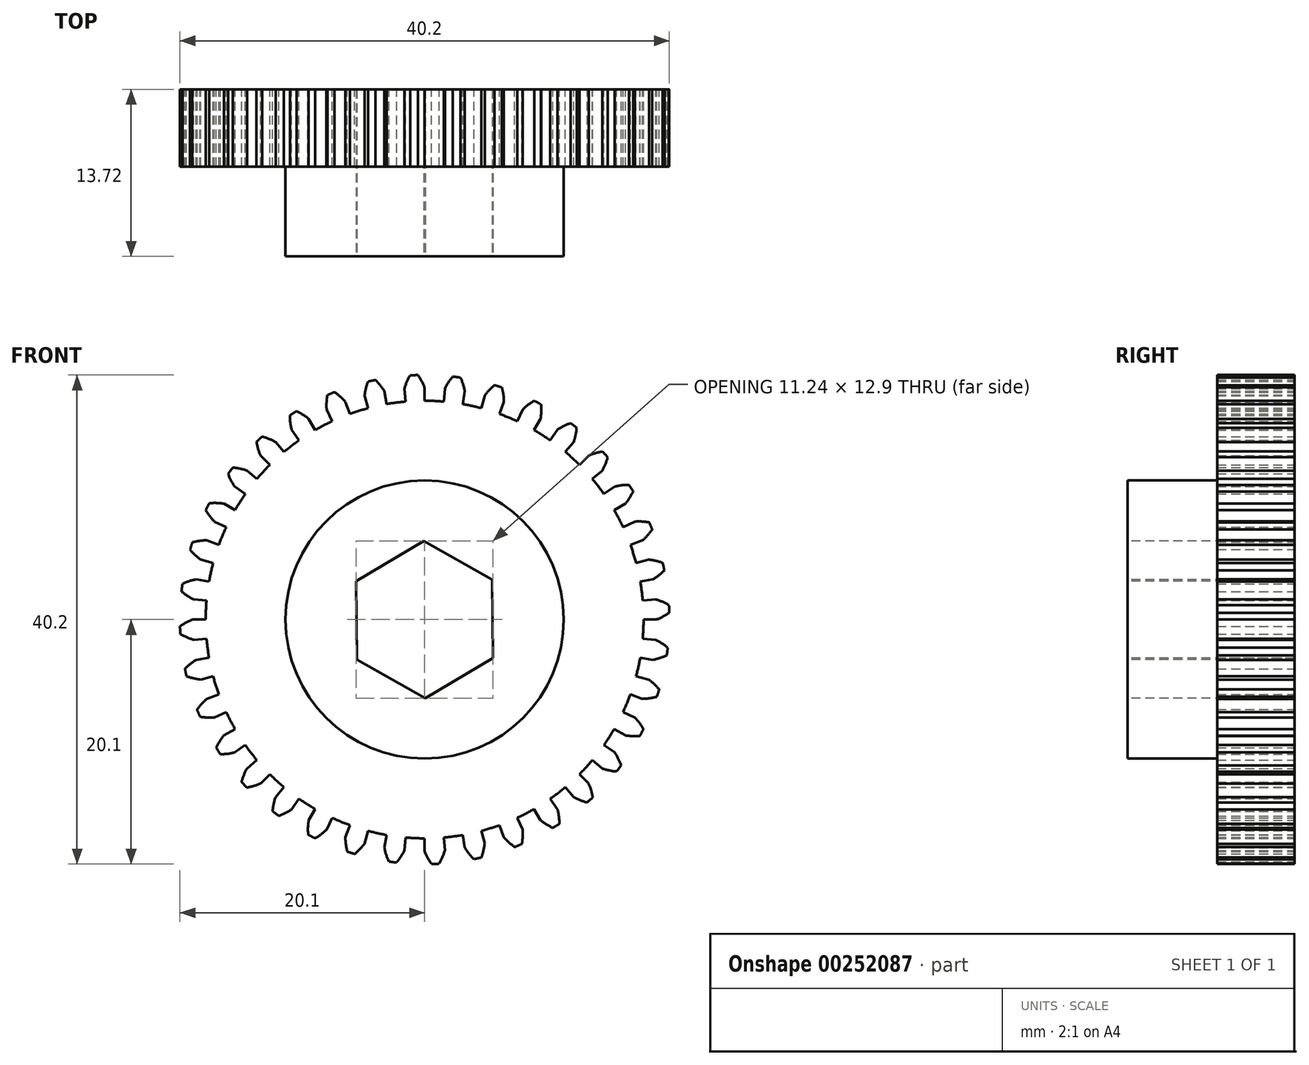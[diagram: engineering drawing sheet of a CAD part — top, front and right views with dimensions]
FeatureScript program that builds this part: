
annotation { "Feature Type Name" : "Feature", "Feature Type Description" : "" }
export const myFeature = defineFeature(function(context is Context, id is Id, definition is map)
    precondition{}
    {
        {
            var Q0;
            Q0=qCreatedBy(makeId("Front.planeOp"),FACE);
            var sketch = newSketch(context, id + "F0", { "sketchPlane" : qUnion([Q0])});
            skArc(sketch, "E0", {"start": v(1.57, 17.91) * mm, "mid": v(0.78, 17.97) * mm, "end": v(0, 17.98) * mm});
            skArc(sketch, "E1", {"start": v(-0.56, 20.1) * mm, "mid": v(-0.72, 20.1) * mm, "end": v(-0.88, 20.08) * mm});
            skLineSegment(sketch, "E2", {"start": v(0, 17.98) * mm, "end": v(0, 19.05) * mm});
            skLineSegment(sketch, "E3", {"start": v(0, 19.05) * mm, "end": v(0, 17.98) * mm});
            skArc(sketch, "E4.trimOffspring", {"start": v(0, 19.05) * mm, "mid": v(-0.25, 19.6) * mm, "end": v(-0.56, 20.1) * mm});
            skPoint(sketch, "E5", {"position": v(0, 17.98) * mm});
            skArc(sketch, "E6.MirrorCS", {"start": v(-1.2, 20.07) * mm, "mid": v(-1.03, 20.08) * mm, "end": v(-0.88, 20.08) * mm});
            skArc(sketch, "E7.MirrorCS", {"start": v(-1.66, 18.98) * mm, "mid": v(-1.46, 19.54) * mm, "end": v(-1.2, 20.07) * mm});
            skLineSegment(sketch, "E8.MirrorCS", {"start": v(-1.66, 18.98) * mm, "end": v(-1.57, 17.91) * mm});
            skLineSegment(sketch, "E9.1.0", {"start": v(-4.93, 18.4) * mm, "end": v(-4.65, 17.37) * mm});
            skArc(sketch, "E9.1.1", {"start": v(-4.93, 18.4) * mm, "mid": v(-4.83, 18.99) * mm, "end": v(-4.66, 19.56) * mm});
            skArc(sketch, "E9.1.2", {"start": v(-3.3, 18.76) * mm, "mid": v(-3.65, 19.25) * mm, "end": v(-4.04, 19.7) * mm});
            skLineSegment(sketch, "E9.1.3", {"start": v(-3.3, 18.76) * mm, "end": v(-3.12, 17.7) * mm});
            skPoint(sketch, "E9.1.4", {"position": v(-3.12, 17.7) * mm});
            skLineSegment(sketch, "E9.1.5", {"start": v(-3.12, 17.7) * mm, "end": v(-3.3, 18.76) * mm});
            skArc(sketch, "E9.1.6", {"start": v(-4.66, 19.56) * mm, "mid": v(-4.5, 19.6) * mm, "end": v(-4.35, 19.63) * mm});
            skArc(sketch, "E9.1.7", {"start": v(-4.04, 19.7) * mm, "mid": v(-4.2, 19.66) * mm, "end": v(-4.35, 19.63) * mm});
            skLineSegment(sketch, "E9.2.0", {"start": v(-8.05, 17.27) * mm, "end": v(-7.6, 16.3) * mm});
            skArc(sketch, "E9.2.1", {"start": v(-8.05, 17.27) * mm, "mid": v(-8.05, 17.86) * mm, "end": v(-7.98, 18.45) * mm});
            skArc(sketch, "E9.2.2", {"start": v(-6.52, 17.9) * mm, "mid": v(-6.93, 18.32) * mm, "end": v(-7.4, 18.7) * mm});
            skLineSegment(sketch, "E9.2.3", {"start": v(-6.52, 17.9) * mm, "end": v(-6.15, 16.9) * mm});
            skPoint(sketch, "E9.2.4", {"position": v(-6.15, 16.9) * mm});
            skLineSegment(sketch, "E9.2.5", {"start": v(-6.15, 16.9) * mm, "end": v(-6.52, 17.9) * mm});
            skArc(sketch, "E9.2.6", {"start": v(-7.98, 18.45) * mm, "mid": v(-7.84, 18.51) * mm, "end": v(-7.7, 18.57) * mm});
            skArc(sketch, "E9.2.7", {"start": v(-7.4, 18.7) * mm, "mid": v(-7.55, 18.63) * mm, "end": v(-7.7, 18.57) * mm});
            skLineSegment(sketch, "E9.3.0", {"start": v(-10.93, 15.6) * mm, "end": v(-10.31, 14.73) * mm});
            skArc(sketch, "E9.3.1", {"start": v(-10.93, 15.6) * mm, "mid": v(-11.03, 16.19) * mm, "end": v(-11.07, 16.78) * mm});
            skArc(sketch, "E9.3.2", {"start": v(-9.52, 16.5) * mm, "mid": v(-10, 16.84) * mm, "end": v(-10.53, 17.12) * mm});
            skLineSegment(sketch, "E9.3.3", {"start": v(-9.52, 16.5) * mm, "end": v(-9, 15.57) * mm});
            skPoint(sketch, "E9.3.4", {"position": v(-9, 15.57) * mm});
            skLineSegment(sketch, "E9.3.5", {"start": v(-9, 15.57) * mm, "end": v(-9.53, 16.5) * mm});
            skArc(sketch, "E9.3.6", {"start": v(-11.07, 16.78) * mm, "mid": v(-10.93, 16.87) * mm, "end": v(-10.8, 16.96) * mm});
            skArc(sketch, "E9.3.7", {"start": v(-10.53, 17.12) * mm, "mid": v(-10.67, 17.04) * mm, "end": v(-10.8, 16.96) * mm});
            skLineSegment(sketch, "E9.4.0", {"start": v(-13.47, 13.47) * mm, "end": v(-12.72, 12.72) * mm});
            skArc(sketch, "E9.4.1", {"start": v(-13.47, 13.47) * mm, "mid": v(-13.68, 14.03) * mm, "end": v(-13.81, 14.6) * mm});
            skArc(sketch, "E9.4.2", {"start": v(-12.25, 14.6) * mm, "mid": v(-12.78, 14.85) * mm, "end": v(-13.35, 15.03) * mm});
            skLineSegment(sketch, "E9.4.3", {"start": v(-12.25, 14.6) * mm, "end": v(-11.56, 13.78) * mm});
            skPoint(sketch, "E9.4.4", {"position": v(-11.56, 13.78) * mm});
            skLineSegment(sketch, "E9.4.5", {"start": v(-11.56, 13.78) * mm, "end": v(-12.25, 14.6) * mm});
            skArc(sketch, "E9.4.6", {"start": v(-13.81, 14.6) * mm, "mid": v(-13.7, 14.72) * mm, "end": v(-13.58, 14.82) * mm});
            skArc(sketch, "E9.4.7", {"start": v(-13.35, 15.03) * mm, "mid": v(-13.47, 14.93) * mm, "end": v(-13.58, 14.82) * mm});
            skLineSegment(sketch, "E9.5.0", {"start": v(-15.6, 10.93) * mm, "end": v(-14.73, 10.31) * mm});
            skArc(sketch, "E9.5.1", {"start": v(-15.6, 10.93) * mm, "mid": v(-15.9, 11.44) * mm, "end": v(-16.14, 11.99) * mm});
            skArc(sketch, "E9.5.2", {"start": v(-14.6, 12.25) * mm, "mid": v(-15.17, 12.4) * mm, "end": v(-15.76, 12.49) * mm});
            skLineSegment(sketch, "E9.5.3", {"start": v(-14.6, 12.25) * mm, "end": v(-13.78, 11.56) * mm});
            skPoint(sketch, "E9.5.4", {"position": v(-13.78, 11.56) * mm});
            skLineSegment(sketch, "E9.5.5", {"start": v(-13.78, 11.56) * mm, "end": v(-14.6, 12.25) * mm});
            skArc(sketch, "E9.5.6", {"start": v(-16.14, 11.99) * mm, "mid": v(-16.05, 12.11) * mm, "end": v(-15.95, 12.24) * mm});
            skArc(sketch, "E9.5.7", {"start": v(-15.76, 12.49) * mm, "mid": v(-15.85, 12.36) * mm, "end": v(-15.95, 12.24) * mm});
            skLineSegment(sketch, "E9.6.0", {"start": v(-17.27, 8.05) * mm, "end": v(-16.3, 7.6) * mm});
            skArc(sketch, "E9.6.1", {"start": v(-17.27, 8.05) * mm, "mid": v(-17.65, 8.5) * mm, "end": v(-17.98, 9) * mm});
            skArc(sketch, "E9.6.2", {"start": v(-16.5, 9.53) * mm, "mid": v(-17.09, 9.58) * mm, "end": v(-17.68, 9.56) * mm});
            skLineSegment(sketch, "E9.6.3", {"start": v(-16.5, 9.53) * mm, "end": v(-15.57, 9) * mm});
            skPoint(sketch, "E9.6.4", {"position": v(-15.57, 9) * mm});
            skLineSegment(sketch, "E9.6.5", {"start": v(-15.57, 9) * mm, "end": v(-16.5, 9.53) * mm});
            skArc(sketch, "E9.6.6", {"start": v(-17.98, 9) * mm, "mid": v(-17.9, 9.14) * mm, "end": v(-17.83, 9.28) * mm});
            skArc(sketch, "E9.6.7", {"start": v(-17.68, 9.56) * mm, "mid": v(-17.76, 9.42) * mm, "end": v(-17.83, 9.28) * mm});
            skLineSegment(sketch, "E9.7.0", {"start": v(-18.4, 4.93) * mm, "end": v(-17.37, 4.65) * mm});
            skArc(sketch, "E9.7.1", {"start": v(-18.4, 4.93) * mm, "mid": v(-18.86, 5.3) * mm, "end": v(-19.27, 5.74) * mm});
            skArc(sketch, "E9.7.2", {"start": v(-17.9, 6.52) * mm, "mid": v(-18.5, 6.47) * mm, "end": v(-19.08, 6.35) * mm});
            skLineSegment(sketch, "E9.7.3", {"start": v(-17.9, 6.52) * mm, "end": v(-16.9, 6.15) * mm});
            skPoint(sketch, "E9.7.4", {"position": v(-16.9, 6.15) * mm});
            skLineSegment(sketch, "E9.7.5", {"start": v(-16.9, 6.15) * mm, "end": v(-17.9, 6.52) * mm});
            skArc(sketch, "E9.7.6", {"start": v(-19.27, 5.74) * mm, "mid": v(-19.22, 5.9) * mm, "end": v(-19.17, 6.05) * mm});
            skArc(sketch, "E9.7.7", {"start": v(-19.08, 6.35) * mm, "mid": v(-19.13, 6.2) * mm, "end": v(-19.17, 6.05) * mm});
            skLineSegment(sketch, "E9.8.0", {"start": v(-18.98, 1.66) * mm, "end": v(-17.91, 1.57) * mm});
            skArc(sketch, "E9.8.1", {"start": v(-18.98, 1.66) * mm, "mid": v(-19.5, 1.95) * mm, "end": v(-19.97, 2.31) * mm});
            skArc(sketch, "E9.8.2", {"start": v(-18.76, 3.3) * mm, "mid": v(-19.34, 3.16) * mm, "end": v(-19.89, 2.94) * mm});
            skLineSegment(sketch, "E9.8.3", {"start": v(-18.76, 3.3) * mm, "end": v(-17.7, 3.12) * mm});
            skPoint(sketch, "E9.8.4", {"position": v(-17.7, 3.12) * mm});
            skLineSegment(sketch, "E9.8.5", {"start": v(-17.7, 3.12) * mm, "end": v(-18.76, 3.3) * mm});
            skArc(sketch, "E9.8.6", {"start": v(-19.97, 2.31) * mm, "mid": v(-19.95, 2.47) * mm, "end": v(-19.93, 2.62) * mm});
            skArc(sketch, "E9.8.7", {"start": v(-19.89, 2.94) * mm, "mid": v(-19.91, 2.78) * mm, "end": v(-19.93, 2.62) * mm});
            skLineSegment(sketch, "E9.9.0", {"start": v(-18.98, -1.66) * mm, "end": v(-17.91, -1.57) * mm});
            skArc(sketch, "E9.9.1", {"start": v(-18.98, -1.66) * mm, "mid": v(-19.54, -1.46) * mm, "end": v(-20.07, -1.2) * mm});
            skArc(sketch, "E9.9.2", {"start": v(-19.05, 0) * mm, "mid": v(-19.6, -0.25) * mm, "end": v(-20.1, -0.56) * mm});
            skLineSegment(sketch, "E9.9.3", {"start": v(-19.05, 0) * mm, "end": v(-17.98, 0) * mm});
            skPoint(sketch, "E9.9.4", {"position": v(-17.98, 0) * mm});
            skLineSegment(sketch, "E9.9.5", {"start": v(-17.98, 0) * mm, "end": v(-19.05, 0) * mm});
            skArc(sketch, "E9.9.6", {"start": v(-20.07, -1.2) * mm, "mid": v(-20.08, -1.03) * mm, "end": v(-20.08, -0.88) * mm});
            skArc(sketch, "E9.9.7", {"start": v(-20.1, -0.56) * mm, "mid": v(-20.1, -0.72) * mm, "end": v(-20.08, -0.88) * mm});
            skLineSegment(sketch, "E9.10.0", {"start": v(-18.4, -4.93) * mm, "end": v(-17.37, -4.65) * mm});
            skArc(sketch, "E9.10.1", {"start": v(-18.4, -4.93) * mm, "mid": v(-18.99, -4.83) * mm, "end": v(-19.56, -4.66) * mm});
            skArc(sketch, "E9.10.2", {"start": v(-18.76, -3.3) * mm, "mid": v(-19.25, -3.65) * mm, "end": v(-19.7, -4.04) * mm});
            skLineSegment(sketch, "E9.10.3", {"start": v(-18.76, -3.3) * mm, "end": v(-17.7, -3.12) * mm});
            skPoint(sketch, "E9.10.4", {"position": v(-17.7, -3.12) * mm});
            skLineSegment(sketch, "E9.10.5", {"start": v(-17.7, -3.12) * mm, "end": v(-18.76, -3.3) * mm});
            skArc(sketch, "E9.10.6", {"start": v(-19.56, -4.66) * mm, "mid": v(-19.6, -4.5) * mm, "end": v(-19.63, -4.35) * mm});
            skArc(sketch, "E9.10.7", {"start": v(-19.7, -4.04) * mm, "mid": v(-19.66, -4.2) * mm, "end": v(-19.63, -4.35) * mm});
            skLineSegment(sketch, "E9.11.0", {"start": v(-17.27, -8.05) * mm, "end": v(-16.3, -7.6) * mm});
            skArc(sketch, "E9.11.1", {"start": v(-17.27, -8.05) * mm, "mid": v(-17.86, -8.05) * mm, "end": v(-18.45, -7.98) * mm});
            skArc(sketch, "E9.11.2", {"start": v(-17.9, -6.52) * mm, "mid": v(-18.32, -6.93) * mm, "end": v(-18.7, -7.4) * mm});
            skLineSegment(sketch, "E9.11.3", {"start": v(-17.9, -6.52) * mm, "end": v(-16.9, -6.15) * mm});
            skPoint(sketch, "E9.11.4", {"position": v(-16.9, -6.15) * mm});
            skLineSegment(sketch, "E9.11.5", {"start": v(-16.9, -6.15) * mm, "end": v(-17.9, -6.52) * mm});
            skArc(sketch, "E9.11.6", {"start": v(-18.45, -7.98) * mm, "mid": v(-18.51, -7.84) * mm, "end": v(-18.57, -7.7) * mm});
            skArc(sketch, "E9.11.7", {"start": v(-18.7, -7.4) * mm, "mid": v(-18.63, -7.55) * mm, "end": v(-18.57, -7.7) * mm});
            skLineSegment(sketch, "E9.12.0", {"start": v(-15.6, -10.93) * mm, "end": v(-14.73, -10.31) * mm});
            skArc(sketch, "E9.12.1", {"start": v(-15.6, -10.93) * mm, "mid": v(-16.19, -11.03) * mm, "end": v(-16.78, -11.07) * mm});
            skArc(sketch, "E9.12.2", {"start": v(-16.5, -9.52) * mm, "mid": v(-16.84, -10) * mm, "end": v(-17.12, -10.53) * mm});
            skLineSegment(sketch, "E9.12.3", {"start": v(-16.5, -9.52) * mm, "end": v(-15.57, -9) * mm});
            skPoint(sketch, "E9.12.4", {"position": v(-15.57, -9) * mm});
            skLineSegment(sketch, "E9.12.5", {"start": v(-15.57, -9) * mm, "end": v(-16.5, -9.53) * mm});
            skArc(sketch, "E9.12.6", {"start": v(-16.78, -11.07) * mm, "mid": v(-16.87, -10.93) * mm, "end": v(-16.96, -10.8) * mm});
            skArc(sketch, "E9.12.7", {"start": v(-17.12, -10.53) * mm, "mid": v(-17.04, -10.67) * mm, "end": v(-16.96, -10.8) * mm});
            skLineSegment(sketch, "E9.13.0", {"start": v(-13.47, -13.47) * mm, "end": v(-12.72, -12.72) * mm});
            skArc(sketch, "E9.13.1", {"start": v(-13.47, -13.47) * mm, "mid": v(-14.03, -13.68) * mm, "end": v(-14.6, -13.81) * mm});
            skArc(sketch, "E9.13.2", {"start": v(-14.6, -12.25) * mm, "mid": v(-14.85, -12.78) * mm, "end": v(-15.03, -13.35) * mm});
            skLineSegment(sketch, "E9.13.3", {"start": v(-14.6, -12.25) * mm, "end": v(-13.78, -11.56) * mm});
            skPoint(sketch, "E9.13.4", {"position": v(-13.78, -11.56) * mm});
            skLineSegment(sketch, "E9.13.5", {"start": v(-13.78, -11.56) * mm, "end": v(-14.6, -12.25) * mm});
            skArc(sketch, "E9.13.6", {"start": v(-14.6, -13.81) * mm, "mid": v(-14.72, -13.7) * mm, "end": v(-14.82, -13.58) * mm});
            skArc(sketch, "E9.13.7", {"start": v(-15.03, -13.35) * mm, "mid": v(-14.93, -13.47) * mm, "end": v(-14.82, -13.58) * mm});
            skLineSegment(sketch, "E9.14.0", {"start": v(-10.93, -15.6) * mm, "end": v(-10.31, -14.73) * mm});
            skArc(sketch, "E9.14.1", {"start": v(-10.93, -15.6) * mm, "mid": v(-11.44, -15.9) * mm, "end": v(-11.99, -16.14) * mm});
            skArc(sketch, "E9.14.2", {"start": v(-12.25, -14.6) * mm, "mid": v(-12.4, -15.17) * mm, "end": v(-12.49, -15.76) * mm});
            skLineSegment(sketch, "E9.14.3", {"start": v(-12.25, -14.6) * mm, "end": v(-11.56, -13.78) * mm});
            skPoint(sketch, "E9.14.4", {"position": v(-11.56, -13.78) * mm});
            skLineSegment(sketch, "E9.14.5", {"start": v(-11.56, -13.78) * mm, "end": v(-12.25, -14.6) * mm});
            skArc(sketch, "E9.14.6", {"start": v(-11.99, -16.14) * mm, "mid": v(-12.11, -16.05) * mm, "end": v(-12.24, -15.95) * mm});
            skArc(sketch, "E9.14.7", {"start": v(-12.49, -15.76) * mm, "mid": v(-12.36, -15.85) * mm, "end": v(-12.24, -15.95) * mm});
            skLineSegment(sketch, "E9.15.0", {"start": v(-8.05, -17.27) * mm, "end": v(-7.6, -16.3) * mm});
            skArc(sketch, "E9.15.1", {"start": v(-8.05, -17.27) * mm, "mid": v(-8.5, -17.65) * mm, "end": v(-9, -17.98) * mm});
            skArc(sketch, "E9.15.2", {"start": v(-9.53, -16.5) * mm, "mid": v(-9.58, -17.09) * mm, "end": v(-9.56, -17.68) * mm});
            skLineSegment(sketch, "E9.15.3", {"start": v(-9.53, -16.5) * mm, "end": v(-9, -15.57) * mm});
            skPoint(sketch, "E9.15.4", {"position": v(-9, -15.57) * mm});
            skLineSegment(sketch, "E9.15.5", {"start": v(-9, -15.57) * mm, "end": v(-9.53, -16.5) * mm});
            skArc(sketch, "E9.15.6", {"start": v(-9, -17.98) * mm, "mid": v(-9.14, -17.9) * mm, "end": v(-9.28, -17.83) * mm});
            skArc(sketch, "E9.15.7", {"start": v(-9.56, -17.68) * mm, "mid": v(-9.42, -17.76) * mm, "end": v(-9.28, -17.83) * mm});
            skLineSegment(sketch, "E9.16.0", {"start": v(-4.93, -18.4) * mm, "end": v(-4.65, -17.37) * mm});
            skArc(sketch, "E9.16.1", {"start": v(-4.93, -18.4) * mm, "mid": v(-5.3, -18.86) * mm, "end": v(-5.74, -19.27) * mm});
            skArc(sketch, "E9.16.2", {"start": v(-6.52, -17.9) * mm, "mid": v(-6.47, -18.5) * mm, "end": v(-6.35, -19.08) * mm});
            skLineSegment(sketch, "E9.16.3", {"start": v(-6.52, -17.9) * mm, "end": v(-6.15, -16.9) * mm});
            skPoint(sketch, "E9.16.4", {"position": v(-6.15, -16.9) * mm});
            skLineSegment(sketch, "E9.16.5", {"start": v(-6.15, -16.9) * mm, "end": v(-6.52, -17.9) * mm});
            skArc(sketch, "E9.16.6", {"start": v(-5.74, -19.27) * mm, "mid": v(-5.9, -19.22) * mm, "end": v(-6.05, -19.17) * mm});
            skArc(sketch, "E9.16.7", {"start": v(-6.35, -19.08) * mm, "mid": v(-6.2, -19.13) * mm, "end": v(-6.05, -19.17) * mm});
            skLineSegment(sketch, "E9.17.0", {"start": v(-1.66, -18.98) * mm, "end": v(-1.57, -17.91) * mm});
            skArc(sketch, "E9.17.1", {"start": v(-1.66, -18.98) * mm, "mid": v(-1.95, -19.5) * mm, "end": v(-2.31, -19.97) * mm});
            skArc(sketch, "E9.17.2", {"start": v(-3.3, -18.76) * mm, "mid": v(-3.16, -19.34) * mm, "end": v(-2.94, -19.89) * mm});
            skLineSegment(sketch, "E9.17.3", {"start": v(-3.3, -18.76) * mm, "end": v(-3.12, -17.7) * mm});
            skPoint(sketch, "E9.17.4", {"position": v(-3.12, -17.7) * mm});
            skLineSegment(sketch, "E9.17.5", {"start": v(-3.12, -17.7) * mm, "end": v(-3.3, -18.76) * mm});
            skArc(sketch, "E9.17.6", {"start": v(-2.31, -19.97) * mm, "mid": v(-2.47, -19.95) * mm, "end": v(-2.62, -19.93) * mm});
            skArc(sketch, "E9.17.7", {"start": v(-2.94, -19.89) * mm, "mid": v(-2.78, -19.91) * mm, "end": v(-2.62, -19.93) * mm});
            skLineSegment(sketch, "E9.18.0", {"start": v(1.66, -18.98) * mm, "end": v(1.57, -17.91) * mm});
            skArc(sketch, "E9.18.1", {"start": v(1.66, -18.98) * mm, "mid": v(1.46, -19.54) * mm, "end": v(1.2, -20.07) * mm});
            skArc(sketch, "E9.18.2", {"start": v(0, -19.05) * mm, "mid": v(0.25, -19.6) * mm, "end": v(0.56, -20.1) * mm});
            skLineSegment(sketch, "E9.18.3", {"start": v(0, -19.05) * mm, "end": v(0, -17.98) * mm});
            skPoint(sketch, "E9.18.4", {"position": v(0, -17.98) * mm});
            skLineSegment(sketch, "E9.18.5", {"start": v(0, -17.98) * mm, "end": v(0, -19.05) * mm});
            skArc(sketch, "E9.18.6", {"start": v(1.2, -20.07) * mm, "mid": v(1.03, -20.08) * mm, "end": v(0.88, -20.08) * mm});
            skArc(sketch, "E9.18.7", {"start": v(0.56, -20.1) * mm, "mid": v(0.72, -20.1) * mm, "end": v(0.88, -20.08) * mm});
            skLineSegment(sketch, "E9.19.0", {"start": v(4.93, -18.4) * mm, "end": v(4.65, -17.37) * mm});
            skArc(sketch, "E9.19.1", {"start": v(4.93, -18.4) * mm, "mid": v(4.83, -18.99) * mm, "end": v(4.66, -19.56) * mm});
            skArc(sketch, "E9.19.2", {"start": v(3.3, -18.76) * mm, "mid": v(3.65, -19.25) * mm, "end": v(4.04, -19.7) * mm});
            skLineSegment(sketch, "E9.19.3", {"start": v(3.3, -18.76) * mm, "end": v(3.12, -17.7) * mm});
            skPoint(sketch, "E9.19.4", {"position": v(3.12, -17.7) * mm});
            skLineSegment(sketch, "E9.19.5", {"start": v(3.12, -17.7) * mm, "end": v(3.3, -18.76) * mm});
            skArc(sketch, "E9.19.6", {"start": v(4.66, -19.56) * mm, "mid": v(4.5, -19.6) * mm, "end": v(4.35, -19.63) * mm});
            skArc(sketch, "E9.19.7", {"start": v(4.04, -19.7) * mm, "mid": v(4.2, -19.66) * mm, "end": v(4.35, -19.63) * mm});
            skLineSegment(sketch, "E9.20.0", {"start": v(8.05, -17.27) * mm, "end": v(7.6, -16.3) * mm});
            skArc(sketch, "E9.20.1", {"start": v(8.05, -17.27) * mm, "mid": v(8.05, -17.86) * mm, "end": v(7.98, -18.45) * mm});
            skArc(sketch, "E9.20.2", {"start": v(6.52, -17.9) * mm, "mid": v(6.93, -18.32) * mm, "end": v(7.4, -18.7) * mm});
            skLineSegment(sketch, "E9.20.3", {"start": v(6.52, -17.9) * mm, "end": v(6.15, -16.9) * mm});
            skPoint(sketch, "E9.20.4", {"position": v(6.15, -16.9) * mm});
            skLineSegment(sketch, "E9.20.5", {"start": v(6.15, -16.9) * mm, "end": v(6.52, -17.9) * mm});
            skArc(sketch, "E9.20.6", {"start": v(7.98, -18.45) * mm, "mid": v(7.84, -18.51) * mm, "end": v(7.7, -18.57) * mm});
            skArc(sketch, "E9.20.7", {"start": v(7.4, -18.7) * mm, "mid": v(7.55, -18.63) * mm, "end": v(7.7, -18.57) * mm});
            skLineSegment(sketch, "E9.21.0", {"start": v(10.93, -15.6) * mm, "end": v(10.31, -14.73) * mm});
            skArc(sketch, "E9.21.1", {"start": v(10.93, -15.6) * mm, "mid": v(11.03, -16.19) * mm, "end": v(11.07, -16.78) * mm});
            skArc(sketch, "E9.21.2", {"start": v(9.52, -16.5) * mm, "mid": v(10, -16.84) * mm, "end": v(10.53, -17.12) * mm});
            skLineSegment(sketch, "E9.21.3", {"start": v(9.53, -16.5) * mm, "end": v(9, -15.57) * mm});
            skPoint(sketch, "E9.21.4", {"position": v(9, -15.57) * mm});
            skLineSegment(sketch, "E9.21.5", {"start": v(9, -15.57) * mm, "end": v(9.53, -16.5) * mm});
            skArc(sketch, "E9.21.6", {"start": v(11.07, -16.78) * mm, "mid": v(10.93, -16.87) * mm, "end": v(10.8, -16.96) * mm});
            skArc(sketch, "E9.21.7", {"start": v(10.53, -17.12) * mm, "mid": v(10.67, -17.04) * mm, "end": v(10.8, -16.96) * mm});
            skLineSegment(sketch, "E9.22.0", {"start": v(13.47, -13.47) * mm, "end": v(12.72, -12.72) * mm});
            skArc(sketch, "E9.22.1", {"start": v(13.47, -13.47) * mm, "mid": v(13.68, -14.03) * mm, "end": v(13.81, -14.6) * mm});
            skArc(sketch, "E9.22.2", {"start": v(12.25, -14.6) * mm, "mid": v(12.78, -14.85) * mm, "end": v(13.35, -15.03) * mm});
            skLineSegment(sketch, "E9.22.3", {"start": v(12.25, -14.6) * mm, "end": v(11.56, -13.78) * mm});
            skPoint(sketch, "E9.22.4", {"position": v(11.56, -13.78) * mm});
            skLineSegment(sketch, "E9.22.5", {"start": v(11.56, -13.78) * mm, "end": v(12.25, -14.6) * mm});
            skArc(sketch, "E9.22.6", {"start": v(13.81, -14.6) * mm, "mid": v(13.7, -14.72) * mm, "end": v(13.58, -14.82) * mm});
            skArc(sketch, "E9.22.7", {"start": v(13.35, -15.03) * mm, "mid": v(13.47, -14.93) * mm, "end": v(13.58, -14.82) * mm});
            skLineSegment(sketch, "E9.23.0", {"start": v(15.6, -10.93) * mm, "end": v(14.73, -10.31) * mm});
            skArc(sketch, "E9.23.1", {"start": v(15.6, -10.93) * mm, "mid": v(15.9, -11.44) * mm, "end": v(16.14, -11.99) * mm});
            skArc(sketch, "E9.23.2", {"start": v(14.6, -12.25) * mm, "mid": v(15.17, -12.4) * mm, "end": v(15.76, -12.49) * mm});
            skLineSegment(sketch, "E9.23.3", {"start": v(14.6, -12.25) * mm, "end": v(13.78, -11.56) * mm});
            skPoint(sketch, "E9.23.4", {"position": v(13.78, -11.56) * mm});
            skLineSegment(sketch, "E9.23.5", {"start": v(13.78, -11.56) * mm, "end": v(14.6, -12.25) * mm});
            skArc(sketch, "E9.23.6", {"start": v(16.14, -11.99) * mm, "mid": v(16.05, -12.11) * mm, "end": v(15.95, -12.24) * mm});
            skArc(sketch, "E9.23.7", {"start": v(15.76, -12.49) * mm, "mid": v(15.85, -12.36) * mm, "end": v(15.95, -12.24) * mm});
            skLineSegment(sketch, "E9.24.0", {"start": v(17.27, -8.05) * mm, "end": v(16.3, -7.6) * mm});
            skArc(sketch, "E9.24.1", {"start": v(17.27, -8.05) * mm, "mid": v(17.65, -8.5) * mm, "end": v(17.98, -9) * mm});
            skArc(sketch, "E9.24.2", {"start": v(16.5, -9.53) * mm, "mid": v(17.09, -9.58) * mm, "end": v(17.68, -9.56) * mm});
            skLineSegment(sketch, "E9.24.3", {"start": v(16.5, -9.53) * mm, "end": v(15.57, -9) * mm});
            skPoint(sketch, "E9.24.4", {"position": v(15.57, -9) * mm});
            skLineSegment(sketch, "E9.24.5", {"start": v(15.57, -9) * mm, "end": v(16.5, -9.53) * mm});
            skArc(sketch, "E9.24.6", {"start": v(17.98, -9) * mm, "mid": v(17.9, -9.14) * mm, "end": v(17.83, -9.28) * mm});
            skArc(sketch, "E9.24.7", {"start": v(17.68, -9.56) * mm, "mid": v(17.76, -9.42) * mm, "end": v(17.83, -9.28) * mm});
            skLineSegment(sketch, "E9.25.0", {"start": v(18.4, -4.93) * mm, "end": v(17.37, -4.65) * mm});
            skArc(sketch, "E9.25.1", {"start": v(18.4, -4.93) * mm, "mid": v(18.86, -5.3) * mm, "end": v(19.27, -5.74) * mm});
            skArc(sketch, "E9.25.2", {"start": v(17.9, -6.52) * mm, "mid": v(18.5, -6.47) * mm, "end": v(19.08, -6.35) * mm});
            skLineSegment(sketch, "E9.25.3", {"start": v(17.9, -6.52) * mm, "end": v(16.9, -6.15) * mm});
            skPoint(sketch, "E9.25.4", {"position": v(16.9, -6.15) * mm});
            skLineSegment(sketch, "E9.25.5", {"start": v(16.9, -6.15) * mm, "end": v(17.9, -6.52) * mm});
            skArc(sketch, "E9.25.6", {"start": v(19.27, -5.74) * mm, "mid": v(19.22, -5.9) * mm, "end": v(19.17, -6.05) * mm});
            skArc(sketch, "E9.25.7", {"start": v(19.08, -6.35) * mm, "mid": v(19.13, -6.2) * mm, "end": v(19.17, -6.05) * mm});
            skLineSegment(sketch, "E9.26.0", {"start": v(18.98, -1.66) * mm, "end": v(17.91, -1.57) * mm});
            skArc(sketch, "E9.26.1", {"start": v(18.98, -1.66) * mm, "mid": v(19.5, -1.95) * mm, "end": v(19.97, -2.31) * mm});
            skArc(sketch, "E9.26.2", {"start": v(18.76, -3.3) * mm, "mid": v(19.34, -3.16) * mm, "end": v(19.89, -2.94) * mm});
            skLineSegment(sketch, "E9.26.3", {"start": v(18.76, -3.3) * mm, "end": v(17.7, -3.12) * mm});
            skPoint(sketch, "E9.26.4", {"position": v(17.7, -3.12) * mm});
            skLineSegment(sketch, "E9.26.5", {"start": v(17.7, -3.12) * mm, "end": v(18.76, -3.3) * mm});
            skArc(sketch, "E9.26.6", {"start": v(19.97, -2.31) * mm, "mid": v(19.95, -2.47) * mm, "end": v(19.93, -2.62) * mm});
            skArc(sketch, "E9.26.7", {"start": v(19.89, -2.94) * mm, "mid": v(19.91, -2.78) * mm, "end": v(19.93, -2.62) * mm});
            skLineSegment(sketch, "E9.27.0", {"start": v(18.98, 1.66) * mm, "end": v(17.91, 1.57) * mm});
            skArc(sketch, "E9.27.1", {"start": v(18.98, 1.66) * mm, "mid": v(19.54, 1.46) * mm, "end": v(20.07, 1.2) * mm});
            skArc(sketch, "E9.27.2", {"start": v(19.05, 0) * mm, "mid": v(19.6, 0.25) * mm, "end": v(20.1, 0.56) * mm});
            skLineSegment(sketch, "E9.27.3", {"start": v(19.05, 0) * mm, "end": v(17.98, 0) * mm});
            skPoint(sketch, "E9.27.4", {"position": v(17.98, 0) * mm});
            skLineSegment(sketch, "E9.27.5", {"start": v(17.98, 0) * mm, "end": v(19.05, 0) * mm});
            skArc(sketch, "E9.27.6", {"start": v(20.07, 1.2) * mm, "mid": v(20.08, 1.03) * mm, "end": v(20.08, 0.88) * mm});
            skArc(sketch, "E9.27.7", {"start": v(20.1, 0.56) * mm, "mid": v(20.1, 0.72) * mm, "end": v(20.08, 0.88) * mm});
            skLineSegment(sketch, "E9.28.0", {"start": v(18.4, 4.93) * mm, "end": v(17.37, 4.65) * mm});
            skArc(sketch, "E9.28.1", {"start": v(18.4, 4.93) * mm, "mid": v(18.99, 4.83) * mm, "end": v(19.56, 4.66) * mm});
            skArc(sketch, "E9.28.2", {"start": v(18.76, 3.3) * mm, "mid": v(19.25, 3.65) * mm, "end": v(19.7, 4.04) * mm});
            skLineSegment(sketch, "E9.28.3", {"start": v(18.76, 3.3) * mm, "end": v(17.7, 3.12) * mm});
            skPoint(sketch, "E9.28.4", {"position": v(17.7, 3.12) * mm});
            skLineSegment(sketch, "E9.28.5", {"start": v(17.7, 3.12) * mm, "end": v(18.76, 3.3) * mm});
            skArc(sketch, "E9.28.6", {"start": v(19.56, 4.66) * mm, "mid": v(19.6, 4.5) * mm, "end": v(19.63, 4.35) * mm});
            skArc(sketch, "E9.28.7", {"start": v(19.7, 4.04) * mm, "mid": v(19.66, 4.2) * mm, "end": v(19.63, 4.35) * mm});
            skLineSegment(sketch, "E9.29.0", {"start": v(17.27, 8.05) * mm, "end": v(16.3, 7.6) * mm});
            skArc(sketch, "E9.29.1", {"start": v(17.27, 8.05) * mm, "mid": v(17.86, 8.05) * mm, "end": v(18.45, 7.98) * mm});
            skArc(sketch, "E9.29.2", {"start": v(17.9, 6.52) * mm, "mid": v(18.32, 6.93) * mm, "end": v(18.7, 7.4) * mm});
            skLineSegment(sketch, "E9.29.3", {"start": v(17.9, 6.52) * mm, "end": v(16.9, 6.15) * mm});
            skPoint(sketch, "E9.29.4", {"position": v(16.9, 6.15) * mm});
            skLineSegment(sketch, "E9.29.5", {"start": v(16.9, 6.15) * mm, "end": v(17.9, 6.52) * mm});
            skArc(sketch, "E9.29.6", {"start": v(18.45, 7.98) * mm, "mid": v(18.51, 7.84) * mm, "end": v(18.57, 7.7) * mm});
            skArc(sketch, "E9.29.7", {"start": v(18.7, 7.4) * mm, "mid": v(18.63, 7.55) * mm, "end": v(18.57, 7.7) * mm});
            skLineSegment(sketch, "E9.30.0", {"start": v(15.6, 10.93) * mm, "end": v(14.73, 10.31) * mm});
            skArc(sketch, "E9.30.1", {"start": v(15.6, 10.93) * mm, "mid": v(16.19, 11.03) * mm, "end": v(16.78, 11.07) * mm});
            skArc(sketch, "E9.30.2", {"start": v(16.5, 9.52) * mm, "mid": v(16.84, 10) * mm, "end": v(17.12, 10.53) * mm});
            skLineSegment(sketch, "E9.30.3", {"start": v(16.5, 9.52) * mm, "end": v(15.57, 9) * mm});
            skPoint(sketch, "E9.30.4", {"position": v(15.57, 9) * mm});
            skLineSegment(sketch, "E9.30.5", {"start": v(15.57, 9) * mm, "end": v(16.5, 9.52) * mm});
            skArc(sketch, "E9.30.6", {"start": v(16.78, 11.07) * mm, "mid": v(16.87, 10.93) * mm, "end": v(16.96, 10.8) * mm});
            skArc(sketch, "E9.30.7", {"start": v(17.12, 10.53) * mm, "mid": v(17.04, 10.67) * mm, "end": v(16.96, 10.8) * mm});
            skLineSegment(sketch, "E9.31.0", {"start": v(13.47, 13.47) * mm, "end": v(12.72, 12.72) * mm});
            skArc(sketch, "E9.31.1", {"start": v(13.47, 13.47) * mm, "mid": v(14.03, 13.68) * mm, "end": v(14.6, 13.81) * mm});
            skArc(sketch, "E9.31.2", {"start": v(14.6, 12.25) * mm, "mid": v(14.85, 12.78) * mm, "end": v(15.03, 13.35) * mm});
            skLineSegment(sketch, "E9.31.3", {"start": v(14.6, 12.25) * mm, "end": v(13.78, 11.56) * mm});
            skPoint(sketch, "E9.31.4", {"position": v(13.78, 11.56) * mm});
            skLineSegment(sketch, "E9.31.5", {"start": v(13.78, 11.56) * mm, "end": v(14.6, 12.25) * mm});
            skArc(sketch, "E9.31.6", {"start": v(14.6, 13.81) * mm, "mid": v(14.72, 13.7) * mm, "end": v(14.82, 13.58) * mm});
            skArc(sketch, "E9.31.7", {"start": v(15.03, 13.35) * mm, "mid": v(14.93, 13.47) * mm, "end": v(14.82, 13.58) * mm});
            skLineSegment(sketch, "E9.32.0", {"start": v(10.93, 15.6) * mm, "end": v(10.31, 14.73) * mm});
            skArc(sketch, "E9.32.1", {"start": v(10.93, 15.6) * mm, "mid": v(11.44, 15.9) * mm, "end": v(11.99, 16.14) * mm});
            skArc(sketch, "E9.32.2", {"start": v(12.25, 14.6) * mm, "mid": v(12.4, 15.17) * mm, "end": v(12.49, 15.76) * mm});
            skLineSegment(sketch, "E9.32.3", {"start": v(12.25, 14.6) * mm, "end": v(11.56, 13.78) * mm});
            skPoint(sketch, "E9.32.4", {"position": v(11.56, 13.78) * mm});
            skLineSegment(sketch, "E9.32.5", {"start": v(11.56, 13.78) * mm, "end": v(12.25, 14.6) * mm});
            skArc(sketch, "E9.32.6", {"start": v(11.99, 16.14) * mm, "mid": v(12.11, 16.05) * mm, "end": v(12.24, 15.95) * mm});
            skArc(sketch, "E9.32.7", {"start": v(12.49, 15.76) * mm, "mid": v(12.36, 15.85) * mm, "end": v(12.24, 15.95) * mm});
            skLineSegment(sketch, "E9.33.0", {"start": v(8.05, 17.27) * mm, "end": v(7.6, 16.3) * mm});
            skArc(sketch, "E9.33.1", {"start": v(8.05, 17.27) * mm, "mid": v(8.5, 17.65) * mm, "end": v(9, 17.98) * mm});
            skArc(sketch, "E9.33.2", {"start": v(9.53, 16.5) * mm, "mid": v(9.58, 17.09) * mm, "end": v(9.56, 17.68) * mm});
            skLineSegment(sketch, "E9.33.3", {"start": v(9.52, 16.5) * mm, "end": v(9, 15.57) * mm});
            skPoint(sketch, "E9.33.4", {"position": v(9, 15.57) * mm});
            skLineSegment(sketch, "E9.33.5", {"start": v(9, 15.57) * mm, "end": v(9.52, 16.5) * mm});
            skArc(sketch, "E9.33.6", {"start": v(9, 17.98) * mm, "mid": v(9.14, 17.9) * mm, "end": v(9.28, 17.83) * mm});
            skArc(sketch, "E9.33.7", {"start": v(9.56, 17.68) * mm, "mid": v(9.42, 17.76) * mm, "end": v(9.28, 17.83) * mm});
            skLineSegment(sketch, "E9.34.0", {"start": v(4.93, 18.4) * mm, "end": v(4.65, 17.37) * mm});
            skArc(sketch, "E9.34.1", {"start": v(4.93, 18.4) * mm, "mid": v(5.3, 18.86) * mm, "end": v(5.74, 19.27) * mm});
            skArc(sketch, "E9.34.2", {"start": v(6.52, 17.9) * mm, "mid": v(6.47, 18.5) * mm, "end": v(6.35, 19.08) * mm});
            skLineSegment(sketch, "E9.34.3", {"start": v(6.52, 17.9) * mm, "end": v(6.15, 16.9) * mm});
            skPoint(sketch, "E9.34.4", {"position": v(6.15, 16.9) * mm});
            skLineSegment(sketch, "E9.34.5", {"start": v(6.15, 16.9) * mm, "end": v(6.52, 17.9) * mm});
            skArc(sketch, "E9.34.6", {"start": v(5.74, 19.27) * mm, "mid": v(5.9, 19.22) * mm, "end": v(6.05, 19.17) * mm});
            skArc(sketch, "E9.34.7", {"start": v(6.35, 19.08) * mm, "mid": v(6.2, 19.13) * mm, "end": v(6.05, 19.17) * mm});
            skLineSegment(sketch, "E9.35.0", {"start": v(1.66, 18.98) * mm, "end": v(1.57, 17.91) * mm});
            skArc(sketch, "E9.35.1", {"start": v(1.66, 18.98) * mm, "mid": v(1.95, 19.5) * mm, "end": v(2.31, 19.97) * mm});
            skArc(sketch, "E9.35.2", {"start": v(3.3, 18.76) * mm, "mid": v(3.16, 19.34) * mm, "end": v(2.94, 19.89) * mm});
            skLineSegment(sketch, "E9.35.3", {"start": v(3.3, 18.76) * mm, "end": v(3.12, 17.7) * mm});
            skPoint(sketch, "E9.35.4", {"position": v(3.12, 17.7) * mm});
            skLineSegment(sketch, "E9.35.5", {"start": v(3.12, 17.7) * mm, "end": v(3.3, 18.76) * mm});
            skArc(sketch, "E9.35.6", {"start": v(2.31, 19.97) * mm, "mid": v(2.47, 19.95) * mm, "end": v(2.62, 19.93) * mm});
            skArc(sketch, "E9.35.7", {"start": v(2.94, 19.89) * mm, "mid": v(2.78, 19.91) * mm, "end": v(2.62, 19.93) * mm});
            skArc(sketch, "E10.trimOffspring", {"start": v(4.65, 17.37) * mm, "mid": v(3.9, 17.56) * mm, "end": v(3.12, 17.7) * mm});
            skArc(sketch, "E11.trimOffspring", {"start": v(7.6, 16.3) * mm, "mid": v(6.88, 16.61) * mm, "end": v(6.15, 16.9) * mm});
            skArc(sketch, "E12.trimOffspring", {"start": v(10.31, 14.73) * mm, "mid": v(9.66, 15.17) * mm, "end": v(9, 15.57) * mm});
            skArc(sketch, "E13.trimOffspring", {"start": v(12.72, 12.72) * mm, "mid": v(12.15, 13.26) * mm, "end": v(11.56, 13.78) * mm});
            skArc(sketch, "E14.trimOffspring", {"start": v(14.73, 10.31) * mm, "mid": v(14.27, 10.95) * mm, "end": v(13.78, 11.56) * mm});
            skArc(sketch, "E15.trimOffspring", {"start": v(16.3, 7.6) * mm, "mid": v(15.95, 8.3) * mm, "end": v(15.57, 9) * mm});
            skArc(sketch, "E16.trimOffspring", {"start": v(17.37, 4.65) * mm, "mid": v(17.15, 5.4) * mm, "end": v(16.9, 6.15) * mm});
            skArc(sketch, "E17.trimOffspring", {"start": v(17.91, 1.57) * mm, "mid": v(17.83, 2.35) * mm, "end": v(17.7, 3.12) * mm});
            skArc(sketch, "E18.trimOffspring", {"start": v(17.91, -1.57) * mm, "mid": v(17.97, -0.78) * mm, "end": v(17.98, 0) * mm});
            skArc(sketch, "E19.trimOffspring", {"start": v(17.37, -4.65) * mm, "mid": v(17.56, -3.9) * mm, "end": v(17.7, -3.12) * mm});
            skArc(sketch, "E20.trimOffspring", {"start": v(16.3, -7.6) * mm, "mid": v(16.61, -6.88) * mm, "end": v(16.9, -6.15) * mm});
            skArc(sketch, "E21.trimOffspring", {"start": v(14.73, -10.31) * mm, "mid": v(15.17, -9.66) * mm, "end": v(15.57, -9) * mm});
            skArc(sketch, "E22.trimOffspring", {"start": v(12.72, -12.72) * mm, "mid": v(13.26, -12.15) * mm, "end": v(13.78, -11.56) * mm});
            skArc(sketch, "E23.trimOffspring", {"start": v(10.31, -14.73) * mm, "mid": v(10.95, -14.27) * mm, "end": v(11.56, -13.78) * mm});
            skArc(sketch, "E24.trimOffspring", {"start": v(7.6, -16.3) * mm, "mid": v(8.3, -15.95) * mm, "end": v(9, -15.57) * mm});
            skArc(sketch, "E25.trimOffspring", {"start": v(4.65, -17.37) * mm, "mid": v(5.4, -17.15) * mm, "end": v(6.15, -16.9) * mm});
            skArc(sketch, "E26.trimOffspring", {"start": v(1.57, -17.91) * mm, "mid": v(2.35, -17.83) * mm, "end": v(3.12, -17.7) * mm});
            skArc(sketch, "E27.trimOffspring", {"start": v(-1.57, -17.91) * mm, "mid": v(-0.78, -17.97) * mm, "end": v(0, -17.98) * mm});
            skArc(sketch, "E28.trimOffspring", {"start": v(-4.65, -17.37) * mm, "mid": v(-3.9, -17.56) * mm, "end": v(-3.12, -17.7) * mm});
            skArc(sketch, "E29.trimOffspring", {"start": v(-7.6, -16.3) * mm, "mid": v(-6.88, -16.61) * mm, "end": v(-6.15, -16.9) * mm});
            skArc(sketch, "E30.trimOffspring", {"start": v(-10.31, -14.73) * mm, "mid": v(-9.66, -15.17) * mm, "end": v(-9, -15.57) * mm});
            skArc(sketch, "E31.trimOffspring", {"start": v(-12.72, -12.72) * mm, "mid": v(-12.15, -13.26) * mm, "end": v(-11.56, -13.78) * mm});
            skArc(sketch, "E32.trimOffspring", {"start": v(-14.73, -10.31) * mm, "mid": v(-14.27, -10.95) * mm, "end": v(-13.78, -11.56) * mm});
            skArc(sketch, "E33.trimOffspring", {"start": v(-16.3, -7.6) * mm, "mid": v(-15.95, -8.3) * mm, "end": v(-15.57, -9) * mm});
            skArc(sketch, "E34.trimOffspring", {"start": v(-17.37, -4.65) * mm, "mid": v(-17.15, -5.4) * mm, "end": v(-16.9, -6.15) * mm});
            skArc(sketch, "E35.trimOffspring", {"start": v(-17.91, -1.57) * mm, "mid": v(-17.83, -2.35) * mm, "end": v(-17.7, -3.12) * mm});
            skArc(sketch, "E36.trimOffspring", {"start": v(-17.91, 1.57) * mm, "mid": v(-17.97, 0.78) * mm, "end": v(-17.98, 0) * mm});
            skArc(sketch, "E37.trimOffspring", {"start": v(-17.37, 4.65) * mm, "mid": v(-17.56, 3.9) * mm, "end": v(-17.7, 3.12) * mm});
            skArc(sketch, "E38.trimOffspring", {"start": v(-16.3, 7.6) * mm, "mid": v(-16.61, 6.88) * mm, "end": v(-16.9, 6.15) * mm});
            skArc(sketch, "E39.trimOffspring", {"start": v(-14.73, 10.31) * mm, "mid": v(-15.17, 9.66) * mm, "end": v(-15.57, 9) * mm});
            skArc(sketch, "E40.trimOffspring", {"start": v(-12.72, 12.72) * mm, "mid": v(-13.26, 12.15) * mm, "end": v(-13.78, 11.56) * mm});
            skArc(sketch, "E41.trimOffspring", {"start": v(-10.31, 14.73) * mm, "mid": v(-10.95, 14.27) * mm, "end": v(-11.56, 13.78) * mm});
            skArc(sketch, "E42.trimOffspring", {"start": v(-7.6, 16.3) * mm, "mid": v(-8.3, 15.95) * mm, "end": v(-9, 15.57) * mm});
            skArc(sketch, "E43.trimOffspring", {"start": v(-4.65, 17.37) * mm, "mid": v(-5.4, 17.15) * mm, "end": v(-6.15, 16.9) * mm});
            skArc(sketch, "E44.trimOffspring", {"start": v(-1.57, 17.91) * mm, "mid": v(-2.35, 17.83) * mm, "end": v(-3.12, 17.7) * mm});
            skSolve(sketch);
        }
        {
            var Q0;
            Q0=makeQuery(id+"F0.imprint","IMPRINT",FACE,{"disambiguationData":[TD([[makeQuery(id+"F0.imprint","IMPRINT",EDGE,{"derivedFrom":sQuery(id+"F0.wireOp",EDGE,"E0")}),1.0]])]});
            extrude(context, id + "F1", {"entities" : qUnion([Q0]), "depth" : 6.35 * mm});
        }
        {
            var Q0;
            Q0=makeQuery(id+"F1.opExtrude","CAP_FACE",FACE,{"disambiguationData":[OSD([sQuery(id+"F0.wireOp",EDGE,"E0"),sQuery(id+"F0.wireOp",EDGE,"E1"),sQuery(id+"F0.wireOp",EDGE,"E3"),sQuery(id+"F0.wireOp",EDGE,"E4.trimOffspring"),sQuery(id+"F0.wireOp",EDGE,"E6.MirrorCS"),sQuery(id+"F0.wireOp",EDGE,"E7.MirrorCS"),sQuery(id+"F0.wireOp",EDGE,"E8.MirrorCS"),sQuery(id+"F0.wireOp",EDGE,"E9.1.0"),sQuery(id+"F0.wireOp",EDGE,"E9.1.1"),sQuery(id+"F0.wireOp",EDGE,"E9.1.2"),sQuery(id+"F0.wireOp",EDGE,"E9.1.5"),sQuery(id+"F0.wireOp",EDGE,"E9.1.6"),sQuery(id+"F0.wireOp",EDGE,"E9.1.7"),sQuery(id+"F0.wireOp",EDGE,"E9.2.0"),sQuery(id+"F0.wireOp",EDGE,"E9.2.1"),sQuery(id+"F0.wireOp",EDGE,"E9.2.2"),sQuery(id+"F0.wireOp",EDGE,"E9.2.5"),sQuery(id+"F0.wireOp",EDGE,"E9.2.6"),sQuery(id+"F0.wireOp",EDGE,"E9.2.7"),sQuery(id+"F0.wireOp",EDGE,"E9.3.0"),sQuery(id+"F0.wireOp",EDGE,"E9.3.1"),sQuery(id+"F0.wireOp",EDGE,"E9.3.2"),sQuery(id+"F0.wireOp",EDGE,"E9.3.5"),sQuery(id+"F0.wireOp",EDGE,"E9.3.6"),sQuery(id+"F0.wireOp",EDGE,"E9.3.7"),sQuery(id+"F0.wireOp",EDGE,"E9.4.0"),sQuery(id+"F0.wireOp",EDGE,"E9.4.1"),sQuery(id+"F0.wireOp",EDGE,"E9.4.2"),sQuery(id+"F0.wireOp",EDGE,"E9.4.5"),sQuery(id+"F0.wireOp",EDGE,"E9.4.6"),sQuery(id+"F0.wireOp",EDGE,"E9.4.7"),sQuery(id+"F0.wireOp",EDGE,"E9.5.0"),sQuery(id+"F0.wireOp",EDGE,"E9.5.1"),sQuery(id+"F0.wireOp",EDGE,"E9.5.2"),sQuery(id+"F0.wireOp",EDGE,"E9.5.5"),sQuery(id+"F0.wireOp",EDGE,"E9.5.6"),sQuery(id+"F0.wireOp",EDGE,"E9.5.7"),sQuery(id+"F0.wireOp",EDGE,"E9.6.0"),sQuery(id+"F0.wireOp",EDGE,"E9.6.1"),sQuery(id+"F0.wireOp",EDGE,"E9.6.2"),sQuery(id+"F0.wireOp",EDGE,"E9.6.5"),sQuery(id+"F0.wireOp",EDGE,"E9.6.6"),sQuery(id+"F0.wireOp",EDGE,"E9.6.7"),sQuery(id+"F0.wireOp",EDGE,"E9.7.0"),sQuery(id+"F0.wireOp",EDGE,"E9.7.1"),sQuery(id+"F0.wireOp",EDGE,"E9.7.2"),sQuery(id+"F0.wireOp",EDGE,"E9.7.5"),sQuery(id+"F0.wireOp",EDGE,"E9.7.6"),sQuery(id+"F0.wireOp",EDGE,"E9.7.7"),sQuery(id+"F0.wireOp",EDGE,"E9.8.0"),sQuery(id+"F0.wireOp",EDGE,"E9.8.1"),sQuery(id+"F0.wireOp",EDGE,"E9.8.2"),sQuery(id+"F0.wireOp",EDGE,"E9.8.5"),sQuery(id+"F0.wireOp",EDGE,"E9.8.6"),sQuery(id+"F0.wireOp",EDGE,"E9.8.7"),sQuery(id+"F0.wireOp",EDGE,"E9.9.0"),sQuery(id+"F0.wireOp",EDGE,"E9.9.1"),sQuery(id+"F0.wireOp",EDGE,"E9.9.2"),sQuery(id+"F0.wireOp",EDGE,"E9.9.5"),sQuery(id+"F0.wireOp",EDGE,"E9.9.6"),sQuery(id+"F0.wireOp",EDGE,"E9.9.7"),sQuery(id+"F0.wireOp",EDGE,"E9.10.0"),sQuery(id+"F0.wireOp",EDGE,"E9.10.1"),sQuery(id+"F0.wireOp",EDGE,"E9.10.2"),sQuery(id+"F0.wireOp",EDGE,"E9.10.5"),sQuery(id+"F0.wireOp",EDGE,"E9.10.6"),sQuery(id+"F0.wireOp",EDGE,"E9.10.7"),sQuery(id+"F0.wireOp",EDGE,"E9.11.0"),sQuery(id+"F0.wireOp",EDGE,"E9.11.1"),sQuery(id+"F0.wireOp",EDGE,"E9.11.2"),sQuery(id+"F0.wireOp",EDGE,"E9.11.5"),sQuery(id+"F0.wireOp",EDGE,"E9.11.6"),sQuery(id+"F0.wireOp",EDGE,"E9.11.7"),sQuery(id+"F0.wireOp",EDGE,"E9.12.0"),sQuery(id+"F0.wireOp",EDGE,"E9.12.1"),sQuery(id+"F0.wireOp",EDGE,"E9.12.2"),sQuery(id+"F0.wireOp",EDGE,"E9.12.5"),sQuery(id+"F0.wireOp",EDGE,"E9.12.6"),sQuery(id+"F0.wireOp",EDGE,"E9.12.7"),sQuery(id+"F0.wireOp",EDGE,"E9.13.0"),sQuery(id+"F0.wireOp",EDGE,"E9.13.1"),sQuery(id+"F0.wireOp",EDGE,"E9.13.2"),sQuery(id+"F0.wireOp",EDGE,"E9.13.5"),sQuery(id+"F0.wireOp",EDGE,"E9.13.6"),sQuery(id+"F0.wireOp",EDGE,"E9.13.7"),sQuery(id+"F0.wireOp",EDGE,"E9.14.0"),sQuery(id+"F0.wireOp",EDGE,"E9.14.1"),sQuery(id+"F0.wireOp",EDGE,"E9.14.2"),sQuery(id+"F0.wireOp",EDGE,"E9.14.5"),sQuery(id+"F0.wireOp",EDGE,"E9.14.6"),sQuery(id+"F0.wireOp",EDGE,"E9.14.7"),sQuery(id+"F0.wireOp",EDGE,"E9.15.0"),sQuery(id+"F0.wireOp",EDGE,"E9.15.1"),sQuery(id+"F0.wireOp",EDGE,"E9.15.2"),sQuery(id+"F0.wireOp",EDGE,"E9.15.5"),sQuery(id+"F0.wireOp",EDGE,"E9.15.6"),sQuery(id+"F0.wireOp",EDGE,"E9.15.7"),sQuery(id+"F0.wireOp",EDGE,"E9.16.0"),sQuery(id+"F0.wireOp",EDGE,"E9.16.1"),sQuery(id+"F0.wireOp",EDGE,"E9.16.2"),sQuery(id+"F0.wireOp",EDGE,"E9.16.5"),sQuery(id+"F0.wireOp",EDGE,"E9.16.6"),sQuery(id+"F0.wireOp",EDGE,"E9.16.7"),sQuery(id+"F0.wireOp",EDGE,"E9.17.0"),sQuery(id+"F0.wireOp",EDGE,"E9.17.1"),sQuery(id+"F0.wireOp",EDGE,"E9.17.2"),sQuery(id+"F0.wireOp",EDGE,"E9.17.5"),sQuery(id+"F0.wireOp",EDGE,"E9.17.6"),sQuery(id+"F0.wireOp",EDGE,"E9.17.7"),sQuery(id+"F0.wireOp",EDGE,"E9.18.0"),sQuery(id+"F0.wireOp",EDGE,"E9.18.1"),sQuery(id+"F0.wireOp",EDGE,"E9.18.2"),sQuery(id+"F0.wireOp",EDGE,"E9.18.5"),sQuery(id+"F0.wireOp",EDGE,"E9.18.6"),sQuery(id+"F0.wireOp",EDGE,"E9.18.7"),sQuery(id+"F0.wireOp",EDGE,"E9.19.0"),sQuery(id+"F0.wireOp",EDGE,"E9.19.1"),sQuery(id+"F0.wireOp",EDGE,"E9.19.2"),sQuery(id+"F0.wireOp",EDGE,"E9.19.5"),sQuery(id+"F0.wireOp",EDGE,"E9.19.6"),sQuery(id+"F0.wireOp",EDGE,"E9.19.7"),sQuery(id+"F0.wireOp",EDGE,"E9.20.0"),sQuery(id+"F0.wireOp",EDGE,"E9.20.1"),sQuery(id+"F0.wireOp",EDGE,"E9.20.2"),sQuery(id+"F0.wireOp",EDGE,"E9.20.5"),sQuery(id+"F0.wireOp",EDGE,"E9.20.6"),sQuery(id+"F0.wireOp",EDGE,"E9.20.7"),sQuery(id+"F0.wireOp",EDGE,"E9.21.0"),sQuery(id+"F0.wireOp",EDGE,"E9.21.1"),sQuery(id+"F0.wireOp",EDGE,"E9.21.2"),sQuery(id+"F0.wireOp",EDGE,"E9.21.5"),sQuery(id+"F0.wireOp",EDGE,"E9.21.6"),sQuery(id+"F0.wireOp",EDGE,"E9.21.7"),sQuery(id+"F0.wireOp",EDGE,"E9.22.0"),sQuery(id+"F0.wireOp",EDGE,"E9.22.1"),sQuery(id+"F0.wireOp",EDGE,"E9.22.2"),sQuery(id+"F0.wireOp",EDGE,"E9.22.5"),sQuery(id+"F0.wireOp",EDGE,"E9.22.6"),sQuery(id+"F0.wireOp",EDGE,"E9.22.7"),sQuery(id+"F0.wireOp",EDGE,"E9.23.0"),sQuery(id+"F0.wireOp",EDGE,"E9.23.1"),sQuery(id+"F0.wireOp",EDGE,"E9.23.2"),sQuery(id+"F0.wireOp",EDGE,"E9.23.5"),sQuery(id+"F0.wireOp",EDGE,"E9.23.6"),sQuery(id+"F0.wireOp",EDGE,"E9.23.7"),sQuery(id+"F0.wireOp",EDGE,"E9.24.0"),sQuery(id+"F0.wireOp",EDGE,"E9.24.1"),sQuery(id+"F0.wireOp",EDGE,"E9.24.2"),sQuery(id+"F0.wireOp",EDGE,"E9.24.5"),sQuery(id+"F0.wireOp",EDGE,"E9.24.6"),sQuery(id+"F0.wireOp",EDGE,"E9.24.7"),sQuery(id+"F0.wireOp",EDGE,"E9.25.0"),sQuery(id+"F0.wireOp",EDGE,"E9.25.1"),sQuery(id+"F0.wireOp",EDGE,"E9.25.2"),sQuery(id+"F0.wireOp",EDGE,"E9.25.5"),sQuery(id+"F0.wireOp",EDGE,"E9.25.6"),sQuery(id+"F0.wireOp",EDGE,"E9.25.7"),sQuery(id+"F0.wireOp",EDGE,"E9.26.0"),sQuery(id+"F0.wireOp",EDGE,"E9.26.1"),sQuery(id+"F0.wireOp",EDGE,"E9.26.2"),sQuery(id+"F0.wireOp",EDGE,"E9.26.5"),sQuery(id+"F0.wireOp",EDGE,"E9.26.6"),sQuery(id+"F0.wireOp",EDGE,"E9.26.7"),sQuery(id+"F0.wireOp",EDGE,"E9.27.0"),sQuery(id+"F0.wireOp",EDGE,"E9.27.1"),sQuery(id+"F0.wireOp",EDGE,"E9.27.2"),sQuery(id+"F0.wireOp",EDGE,"E9.27.5"),sQuery(id+"F0.wireOp",EDGE,"E9.27.6"),sQuery(id+"F0.wireOp",EDGE,"E9.27.7"),sQuery(id+"F0.wireOp",EDGE,"E9.28.0"),sQuery(id+"F0.wireOp",EDGE,"E9.28.1"),sQuery(id+"F0.wireOp",EDGE,"E9.28.2"),sQuery(id+"F0.wireOp",EDGE,"E9.28.5"),sQuery(id+"F0.wireOp",EDGE,"E9.28.6"),sQuery(id+"F0.wireOp",EDGE,"E9.28.7"),sQuery(id+"F0.wireOp",EDGE,"E9.29.0"),sQuery(id+"F0.wireOp",EDGE,"E9.29.1"),sQuery(id+"F0.wireOp",EDGE,"E9.29.2"),sQuery(id+"F0.wireOp",EDGE,"E9.29.5"),sQuery(id+"F0.wireOp",EDGE,"E9.29.6"),sQuery(id+"F0.wireOp",EDGE,"E9.29.7"),sQuery(id+"F0.wireOp",EDGE,"E9.30.0"),sQuery(id+"F0.wireOp",EDGE,"E9.30.1"),sQuery(id+"F0.wireOp",EDGE,"E9.30.2"),sQuery(id+"F0.wireOp",EDGE,"E9.30.5"),sQuery(id+"F0.wireOp",EDGE,"E9.30.6"),sQuery(id+"F0.wireOp",EDGE,"E9.30.7"),sQuery(id+"F0.wireOp",EDGE,"E9.31.0"),sQuery(id+"F0.wireOp",EDGE,"E9.31.1"),sQuery(id+"F0.wireOp",EDGE,"E9.31.2"),sQuery(id+"F0.wireOp",EDGE,"E9.31.5"),sQuery(id+"F0.wireOp",EDGE,"E9.31.6"),sQuery(id+"F0.wireOp",EDGE,"E9.31.7"),sQuery(id+"F0.wireOp",EDGE,"E9.32.0"),sQuery(id+"F0.wireOp",EDGE,"E9.32.1"),sQuery(id+"F0.wireOp",EDGE,"E9.32.2"),sQuery(id+"F0.wireOp",EDGE,"E9.32.5"),sQuery(id+"F0.wireOp",EDGE,"E9.32.6"),sQuery(id+"F0.wireOp",EDGE,"E9.32.7"),sQuery(id+"F0.wireOp",EDGE,"E9.33.0"),sQuery(id+"F0.wireOp",EDGE,"E9.33.1"),sQuery(id+"F0.wireOp",EDGE,"E9.33.2"),sQuery(id+"F0.wireOp",EDGE,"E9.33.5"),sQuery(id+"F0.wireOp",EDGE,"E9.33.6"),sQuery(id+"F0.wireOp",EDGE,"E9.33.7"),sQuery(id+"F0.wireOp",EDGE,"E9.34.0"),sQuery(id+"F0.wireOp",EDGE,"E9.34.1"),sQuery(id+"F0.wireOp",EDGE,"E9.34.2"),sQuery(id+"F0.wireOp",EDGE,"E9.34.5"),sQuery(id+"F0.wireOp",EDGE,"E9.34.6"),sQuery(id+"F0.wireOp",EDGE,"E9.34.7"),sQuery(id+"F0.wireOp",EDGE,"E9.35.0"),sQuery(id+"F0.wireOp",EDGE,"E9.35.1"),sQuery(id+"F0.wireOp",EDGE,"E9.35.2"),sQuery(id+"F0.wireOp",EDGE,"E9.35.5"),sQuery(id+"F0.wireOp",EDGE,"E9.35.6"),sQuery(id+"F0.wireOp",EDGE,"E9.35.7"),sQuery(id+"F0.wireOp",EDGE,"E10.trimOffspring"),sQuery(id+"F0.wireOp",EDGE,"E11.trimOffspring"),sQuery(id+"F0.wireOp",EDGE,"E12.trimOffspring"),sQuery(id+"F0.wireOp",EDGE,"E13.trimOffspring"),sQuery(id+"F0.wireOp",EDGE,"E14.trimOffspring"),sQuery(id+"F0.wireOp",EDGE,"E15.trimOffspring"),sQuery(id+"F0.wireOp",EDGE,"E16.trimOffspring"),sQuery(id+"F0.wireOp",EDGE,"E17.trimOffspring"),sQuery(id+"F0.wireOp",EDGE,"E18.trimOffspring"),sQuery(id+"F0.wireOp",EDGE,"E19.trimOffspring"),sQuery(id+"F0.wireOp",EDGE,"E20.trimOffspring"),sQuery(id+"F0.wireOp",EDGE,"E21.trimOffspring"),sQuery(id+"F0.wireOp",EDGE,"E22.trimOffspring"),sQuery(id+"F0.wireOp",EDGE,"E23.trimOffspring"),sQuery(id+"F0.wireOp",EDGE,"E24.trimOffspring"),sQuery(id+"F0.wireOp",EDGE,"E25.trimOffspring"),sQuery(id+"F0.wireOp",EDGE,"E26.trimOffspring"),sQuery(id+"F0.wireOp",EDGE,"E27.trimOffspring"),sQuery(id+"F0.wireOp",EDGE,"E28.trimOffspring"),sQuery(id+"F0.wireOp",EDGE,"E29.trimOffspring"),sQuery(id+"F0.wireOp",EDGE,"E30.trimOffspring"),sQuery(id+"F0.wireOp",EDGE,"E31.trimOffspring"),sQuery(id+"F0.wireOp",EDGE,"E32.trimOffspring"),sQuery(id+"F0.wireOp",EDGE,"E33.trimOffspring"),sQuery(id+"F0.wireOp",EDGE,"E34.trimOffspring"),sQuery(id+"F0.wireOp",EDGE,"E35.trimOffspring"),sQuery(id+"F0.wireOp",EDGE,"E36.trimOffspring"),sQuery(id+"F0.wireOp",EDGE,"E37.trimOffspring"),sQuery(id+"F0.wireOp",EDGE,"E38.trimOffspring"),sQuery(id+"F0.wireOp",EDGE,"E39.trimOffspring"),sQuery(id+"F0.wireOp",EDGE,"E40.trimOffspring"),sQuery(id+"F0.wireOp",EDGE,"E41.trimOffspring"),sQuery(id+"F0.wireOp",EDGE,"E42.trimOffspring"),sQuery(id+"F0.wireOp",EDGE,"E43.trimOffspring"),sQuery(id+"F0.wireOp",EDGE,"E44.trimOffspring")])],"isStart":false});
            var sketch = newSketch(context, id + "F2", { "sketchPlane" : qUnion([Q0])});
            skCircle(sketch, "E45", {"center": v(0, 0) * mm, "radius": 11.43 * mm});
            skSolve(sketch);
        }
        {
            var Q0;
            Q0=makeQuery(id+"F2.imprint","IMPRINT",FACE,{"disambiguationData":[TD([[makeQuery(id+"F2.imprint","IMPRINT",EDGE,{"derivedFrom":sQuery(id+"F2.wireOp",EDGE,"E45")}),1.0]])]});
            extrude(context, id + "F3", {"entities" : qUnion([Q0]), "operationType" : NewBodyOperationType.ADD, "depth" : 7.37 * mm});
        }
        {
            var Q0;
            Q0=makeQuery(id+"F3.opExtrude","CAP_FACE",FACE,{"disambiguationData":[OSD([sQuery(id+"F2.wireOp",EDGE,"E45")])],"isStart":false});
            var sketch = newSketch(context, id + "F4", { "sketchPlane" : qUnion([Q0])});
            skCircle(sketch, "E46.cCircle", {"center": v(0, 0) * mm, "radius": 5.59 * mm, "construction": true});
            skLineSegment(sketch, "E46.0", {"start": v(5.62, -3.17) * mm, "end": v(0.07, -6.45) * mm});
            skLineSegment(sketch, "E46.1", {"start": v(0.07, -6.45) * mm, "end": v(-5.55, -3.28) * mm});
            skLineSegment(sketch, "E46.2", {"start": v(-5.55, -3.28) * mm, "end": v(-5.62, 3.17) * mm});
            skLineSegment(sketch, "E46.3", {"start": v(-5.62, 3.17) * mm, "end": v(-0.07, 6.45) * mm});
            skLineSegment(sketch, "E46.4", {"start": v(-0.07, 6.45) * mm, "end": v(5.55, 3.28) * mm});
            skLineSegment(sketch, "E46.5", {"start": v(5.55, 3.28) * mm, "end": v(5.62, -3.17) * mm});
            skPoint(sketch, "E46.0.midPoint", {"position": v(2.84, -4.81) * mm});
            skSolve(sketch);
        }
        {
            var Q0;
            Q0=makeQuery(id+"F4.imprint","IMPRINT",FACE,{"disambiguationData":[TD([[makeQuery(id+"F4.imprint","IMPRINT",EDGE,{"derivedFrom":sQuery(id+"F4.wireOp",EDGE,"E46.0")}),-1.0]])]});
            extrude(context, id + "F5", {"entities" : qUnion([Q0]), "operationType" : NewBodyOperationType.REMOVE, "oppositeDirection" : true, "depth" : 25.4 * mm});
        }
    });
